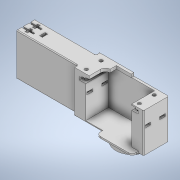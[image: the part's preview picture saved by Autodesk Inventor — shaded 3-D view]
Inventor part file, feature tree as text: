
AUTODESK INVENTOR PART (.ipt)
format: ipt  version: 2022 (Build 260153000, 153)  size: 722,944 bytes
history: native  units: mm
features: sketch x25, extrude x24, fillet x9, projected_geometry x9, other x8, mirror x1, pattern_circular x1
ambient origin geometry x8: Origin, YZ Plane, XZ Plane, XY Plane, X Axis, Y Axis, Z Axis, Center Point
bodies: Body1 (feature_tree)
feature tree (77):
  other  "Твердое тело1"
  extrude  "Выдавливание1"  Depth=29.25mm
  extrude  "Выдавливание2"  Depth=59.05mm
  extrude  "Выдавливание3"  Depth=15.0mm
  other  "РабПлоскость1"
  extrude  "Выдавливание4"  Depth=3.0mm
  other  "РабПлоскость2"
  other  "РабПлоскость3"
  other  "РабПлоскость5"
  extrude  "Выдавливание10"  Depth=41.0mm TaperAngle=0.0deg
  extrude  "Выдавливание11"  Depth=2.0mm TaperAngle=0.0deg
  fillet  "Сопряжение8"  Radius=4.2mm
  extrude  "Выдавливание12"  Depth=20.0mm TaperAngle=0.0deg
  fillet  "Сопряжение9"  [1 undecoded]
  mirror  "Зеркальное отражение2"
  extrude  "Выдавливание13"  Depth=7.15mm
  extrude  "Выдавливание15"  Depth=20.0mm
  sketch  "Эскиз18"
  other  "РабОсь1"
  extrude  "Выдавливание16"  Depth=3.25mm TaperAngle=0.0deg
  fillet  "Сопряжение12"  Radius=7.0mm
  pattern_circular  "Круговой массив1"  [2 undecoded]
  fillet  "Сопряжение14"  Radius=4.0mm
  extrude  "Выдавливание24"  Depth=1.95mm
  extrude  "Выдавливание25"  Depth=10.0mm
  extrude  "Выдавливание26"  Depth=2.0mm
  other  "РабПлоскость8"
  extrude  "Выдавливание27"  Depth=1.5mm TaperAngle=0.0deg
  extrude  "Выдавливание28"  Depth=1.0mm
  extrude  "Выдавливание29"  Depth=0.2mm
  extrude  "Выдавливание30"  Depth=19.0mm
  fillet  "Сопряжение18"  Radius=68.0mm
  fillet  "Сопряжение19"  Radius=3.5mm
  extrude  "Выдавливание17"  Depth=5.0mm
  fillet  "Сопряжение15"  Radius=4.1mm
  extrude  "Выдавливание18"  Depth=7.95mm
  extrude  "Выдавливание19"  Depth=28.1mm
  extrude  "Выдавливание20"  Depth=4.0mm TaperAngle=0.0deg
  extrude  "Выдавливание21"  Depth=18.75mm
  fillet  "Сопряжение16"  Radius=37.8mm
  extrude  "Выдавливание22"  Depth=2.0mm
  other  "РабПлоскость7"
  extrude  "Выдавливание23"  Depth=6.0mm TaperAngle=0.0deg
  fillet  "Сопряжение17"  Radius=0.5mm
  sketch  "Эскиз14"
  sketch  "Эскиз1"
  sketch  "Эскиз2"
  sketch  "Эскиз3"
  sketch  "Эскиз4"
  sketch  "Эскиз10"
  sketch  "Эскиз11"
  sketch  "Эскиз13"
  sketch  "Эскиз15"
  sketch  "Эскиз17"
  sketch  "Эскиз19"
  projected_geometry  "Спроецированная петля1"
  sketch  "Эскиз20"
  projected_geometry  "Спроецированная петля2"
  sketch  "Эскиз21"
  projected_geometry  "Спроецированная петля3"
  sketch  "Эскиз22"
  sketch  "Эскиз23"
  sketch  "Эскиз25"
  projected_geometry  "Спроецированная петля4"
  sketch  "Эскиз26"
  projected_geometry  "Спроецированная петля5"
  sketch  "Эскиз27"
  projected_geometry  "Спроецированная петля6"
  sketch  "Эскиз28"
  projected_geometry  "Спроецированная петля7"
  sketch  "Эскиз29"
  projected_geometry  "Спроецированная петля8"
  sketch  "Эскиз30"
  sketch  "Эскиз31"
  projected_geometry  "Спроецированная петля9"
  sketch  "Эскиз32"
  sketch  "Эскиз33"
note: 3 required parameter values undecoded (feature->parameter linkage not recoverable at this tier; creation-order binding heuristic only, values carry confidence <= 0.55)
